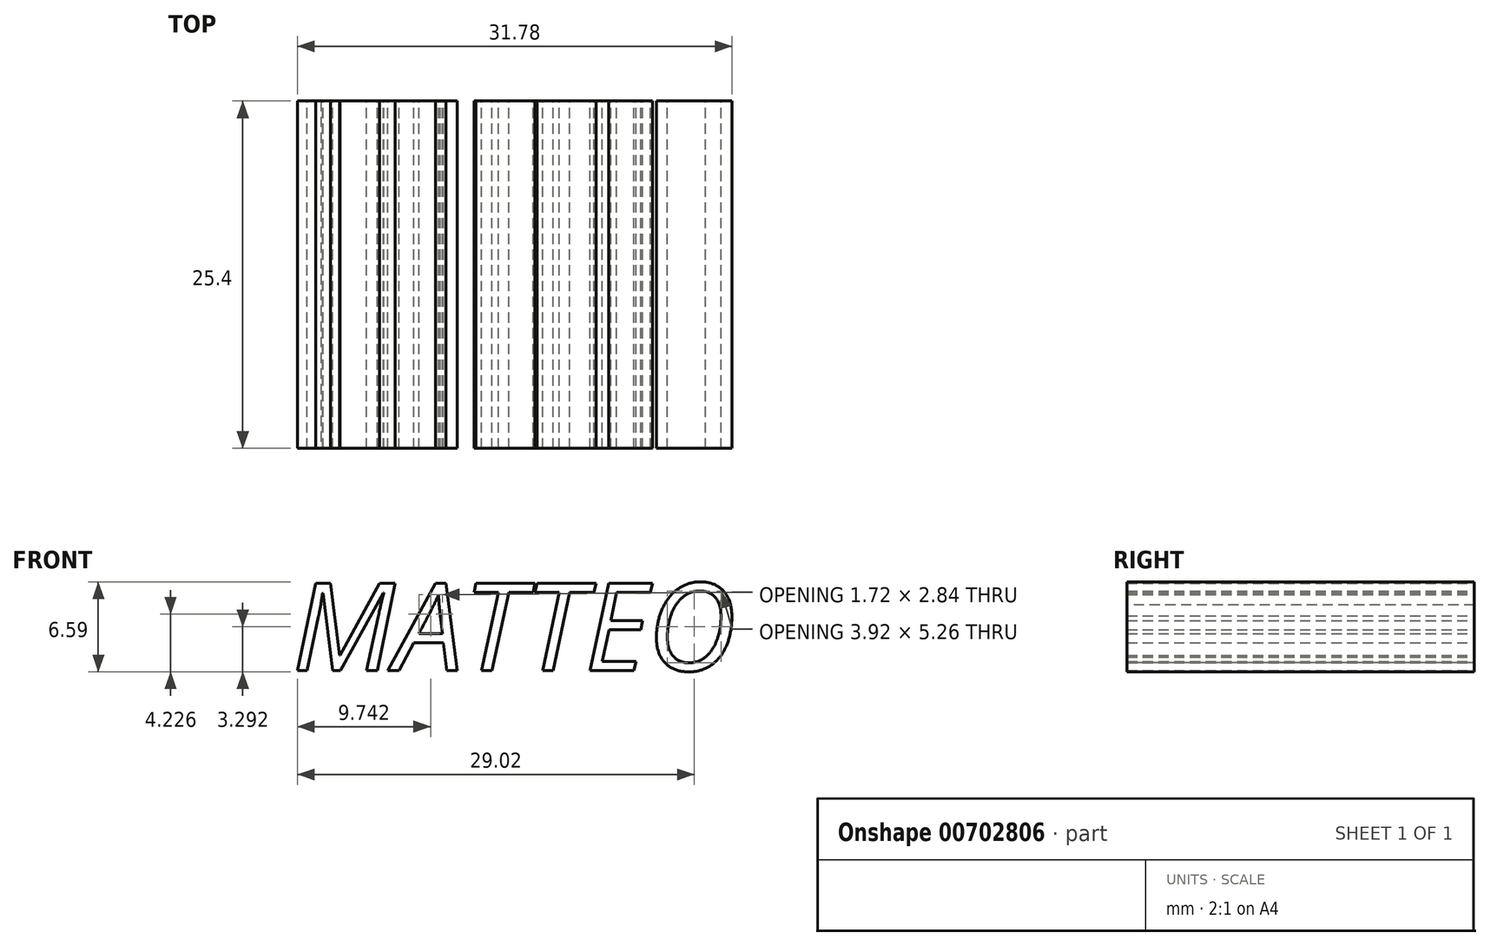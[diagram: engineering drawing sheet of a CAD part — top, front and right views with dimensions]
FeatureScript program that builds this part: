
annotation { "Feature Type Name" : "Feature", "Feature Type Description" : "" }
export const myFeature = defineFeature(function(context is Context, id is Id, definition is map)
    precondition{}
    {
        {
            var Q0;
            Q0=qCreatedBy(makeId("Front.planeOp"),FACE);
            var sketch = newSketch(context, id + "F0", { "sketchPlane" : qUnion([Q0])});
            skText(sketch, "E0", { "text": "MATTEO", "fontName": "OpenSans-Italic.ttf"});
            const initialGuessF0  = {"E0": [-0.06036, 0.02912, 1, 0, 0.00645]};
            skSetInitialGuess(sketch, initialGuessF0);
            skSolve(sketch);
        }
        {
            var Q0;
            Q0 = qSketchRegion(id + "F0", true);
            extrude(context, id + "F1", {"entities" : qUnion([Q0]), "depth" : 25.4 * mm, "offsetDistance" : 25.4 * mm});
        }
    });
